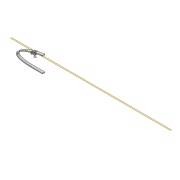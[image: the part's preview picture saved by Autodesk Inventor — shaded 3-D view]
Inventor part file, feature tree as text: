
AUTODESK INVENTOR PART (.ipt)
format: ipt  version: 2022 (Build 260153000, 153)  size: 660,992 bytes
history: native  units: mm
features: extrude x13, sketch x11, projected_geometry x9, plane x4, shell x1, fillet x1
ambient origin geometry x8: Origin, YZ Plane, XZ Plane, XY Plane, X Axis, Y Axis, Z Axis, Center Point
bodies: Solid1 (feature_tree)
feature tree (39):
  extrude  "Extrusion1"  Depth=3.0mm
  shell  "Shell1"  Thickness=5.215mm
  plane  "Work Plane3"
  sketch  "Sketch26"  dims[d69=4.1mm d70=63.6mm]
  plane  "Work Plane4"
  extrude  "Extrusion9"  Depth=63.6mm
  plane  "Work Plane5"
  sketch  "Sketch38"  dims[d88=2.0mm d89=4.0mm]
  extrude  "Extrusion10"  Depth=4.2mm
  extrude  "Extrusion11"  Depth=6.0mm
  extrude  "Extrusion12"  Depth=21.0mm TaperAngle=0.0deg
  plane  "Work Plane6"
  extrude  "Extrusion13"  Depth=5.0mm
  extrude  "Extrusion15"  Depth=3.0mm TaperAngle=0.0deg
  extrude  "Extrusion16"  Depth=2.0mm
  extrude  "Extrusion17"  Depth=4.0mm
  extrude  "Extrusion20"  Depth=3.0mm TaperAngle=0.0deg
  fillet  "Fillet2"  Radius=12.0mm
  extrude  "Extrusion18"  Depth=28.0mm
  extrude  "Extrusion21"  Depth=9.0mm TaperAngle=0.0deg
  extrude  "Extrusion22"  Depth=200.0mm
  sketch  "Sketch3"  dims[d0=12.0mm d1=0.0mm d2=3.0mm d68=5.215mm]
  sketch  "Sketch27"  dims[d71=16.0mm d72=4.2mm]
  projected_geometry  "Projected Loop13"
  sketch  "Sketch29"  dims[d73=63.6mm d74=6.0mm]
  sketch  "Sketch30"  dims[d75=7.0mm d76=21.0mm d77=0.0mm]
  projected_geometry  "Projected Loop14"
  sketch  "Sketch31"  dims[d78=-11.0mm d79=5.0mm]
  projected_geometry  "Projected Loop15"
  projected_geometry  "Projected Loop16"
  projected_geometry  "Projected Loop17"
  sketch  "Sketch33"  dims[d80=10.0mm d83=3.0mm d84=0.0mm]
  projected_geometry  "Projected Loop18"
  projected_geometry  "Projected Loop19"
  sketch  "Sketch36"  dims[d86=0.65mm d87=2.0mm]
  projected_geometry  "Projected Loop20"
  sketch  "Sketch39"  dims[d90=4.0mm d91=3.0mm d92=0.0mm d93=12.0mm]
  sketch  "Sketch41"  dims[d94=6.5mm d95=0.0mm d96=28.0mm d98=9.0mm d99=0.0mm d103=200.0mm d104=100.0mm d105=0.0mm d106=7.0mm d107=4.1mm d108=7.0mm d109=2.0mm d110=0.0mm d111=2.0mm d112=0.0mm d113=2.0mm d114=95.0mm d115=10.0mm d116=0.0mm d119=100.0mm d120=0.0mm d121=1.0mm d122=3.0mm d123=0.0mm d124=10.0mm d125=0.0mm]
  projected_geometry  "Project Cut Edges1"
